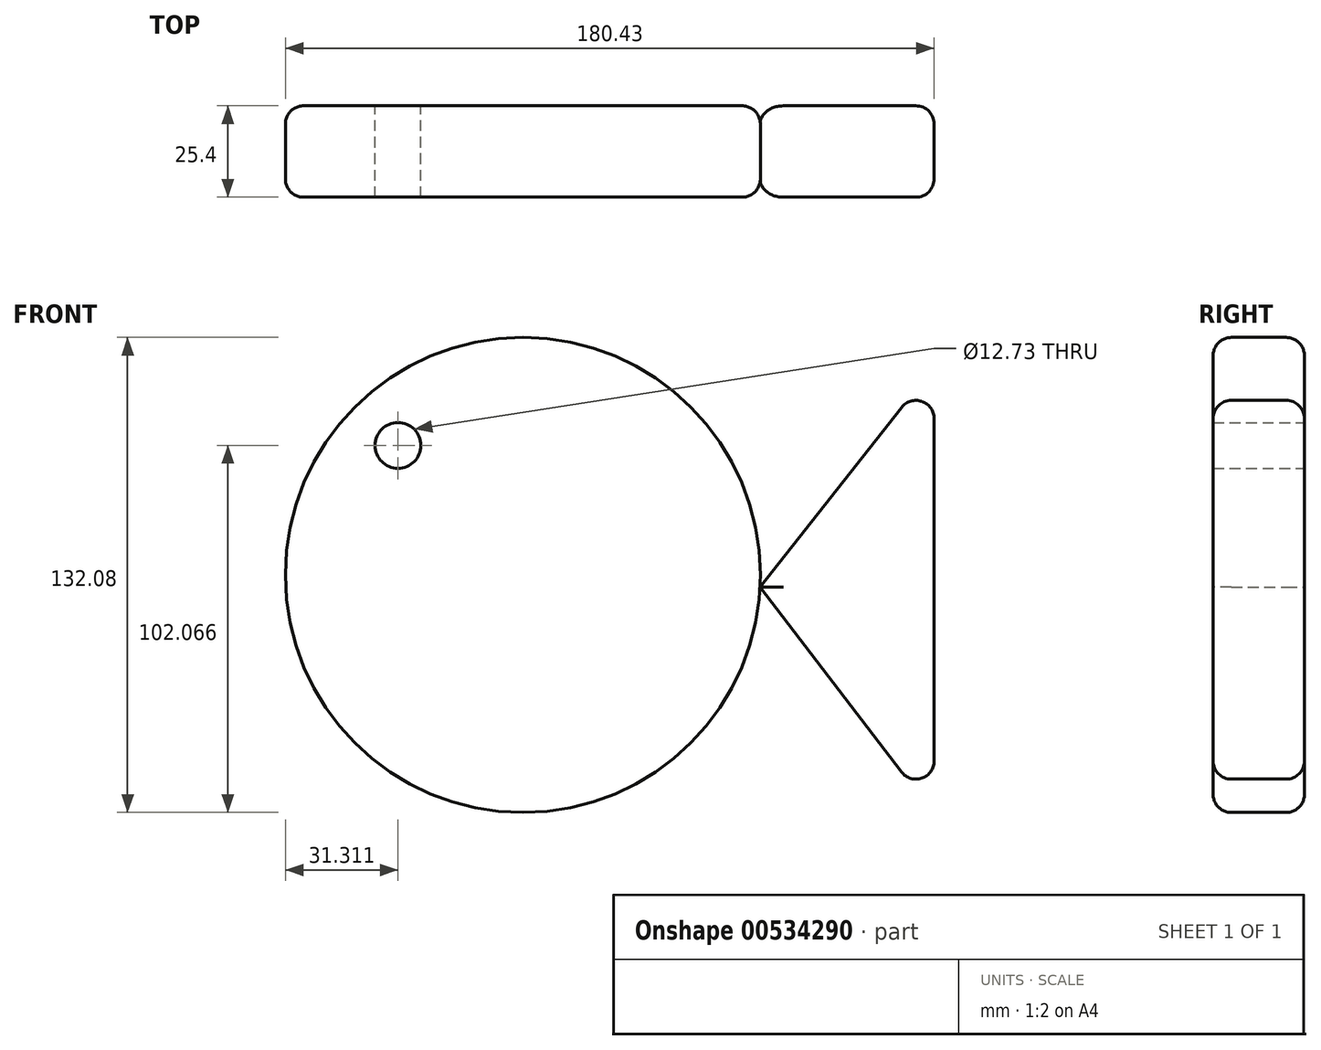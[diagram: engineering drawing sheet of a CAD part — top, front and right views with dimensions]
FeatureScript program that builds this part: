
annotation { "Feature Type Name" : "Feature", "Feature Type Description" : "" }
export const myFeature = defineFeature(function(context is Context, id is Id, definition is map)
    precondition{}
    {
        {
            var Q0;
            Q0=qCreatedBy(makeId("Front.planeOp"),FACE);
            var sketch = newSketch(context, id + "F0", { "sketchPlane" : qUnion([Q0])});
            skCircle(sketch, "E0", {"center": v(0, 0) * mm, "radius": 66.04 * mm});
            skLineSegment(sketch, "E1", {"start": v(65.95, -3.38) * mm, "end": v(114.39, 58.12) * mm});
            skLineSegment(sketch, "E2", {"start": v(114.39, 58.12) * mm, "end": v(114.39, -66.7) * mm});
            skLineSegment(sketch, "E3", {"start": v(114.39, -66.7) * mm, "end": v(65.95, -3.38) * mm});
            skSolve(sketch);
        }
        {
            var Q0;
            Q0=makeQuery(id+"F0.imprint","IMPRINT",FACE,{"disambiguationData":[TD([[makeQuery(id+"F0.imprint","IMPRINT",EDGE,{"derivedFrom":sQuery(id+"F0.wireOp",EDGE,"E0")}),1.0]])]});
            var Q1;
            Q1=makeQuery(id+"F0.imprint","IMPRINT",FACE,{"disambiguationData":[TD([[makeQuery(id+"F0.imprint","IMPRINT",EDGE,{"derivedFrom":sQuery(id+"F0.wireOp",EDGE,"E1")}),-1.0]])]});
            extrude(context, id + "F1", {"entities" : qUnion([Q0, Q1]), "depth" : 25.4 * mm, "offsetDistance" : 25.4 * mm});
        }
        {
            var Q0;
            Q0=makeQuery(id+"F1.opExtrude","CAP_EDGE",EDGE,{"disambiguationData":[OSD([sQuery(id+"F0.wireOp",EDGE,"E0")])],"isStart":false});
            var Q1;
            Q1=makeQuery(id+"F1.opExtrude","CAP_EDGE",EDGE,{"disambiguationData":[OSD([sQuery(id+"F0.wireOp",EDGE,"E0")])],"isStart":true});
            var Q2;
            Q2=makeQuery(id+"F1.opExtrude","CAP_EDGE",EDGE,{"disambiguationData":[OSD([sQuery(id+"F0.wireOp",EDGE,"E1")])],"isStart":false});
            var Q3;
            Q3=makeQuery(id+"F1.opExtrude","SWEPT_EDGE",EDGE,{"disambiguationData":[OSD([sQuery(id+"F0.wireOp",EDGE,"E1"),sQuery(id+"F0.wireOp",EDGE,"E2")])]});
            var Q4;
            Q4=makeQuery(id+"F1.opExtrude","CAP_EDGE",EDGE,{"disambiguationData":[OSD([sQuery(id+"F0.wireOp",EDGE,"E2")])],"isStart":true});
            var Q5;
            Q5=makeQuery(id+"F1.opExtrude","SWEPT_EDGE",EDGE,{"disambiguationData":[OSD([sQuery(id+"F0.wireOp",EDGE,"E2"),sQuery(id+"F0.wireOp",EDGE,"E3")])]});
            var Q6;
            Q6=makeQuery(id+"F1.opExtrude","CAP_EDGE",EDGE,{"disambiguationData":[OSD([sQuery(id+"F0.wireOp",EDGE,"E3")])],"isStart":false});
            var Q7;
            Q7=makeQuery(id+"F1.opExtrude","CAP_EDGE",EDGE,{"disambiguationData":[OSD([sQuery(id+"F0.wireOp",EDGE,"E2")])],"isStart":false});
            var Q8;
            Q8=makeQuery(id+"F1.opExtrude","CAP_EDGE",EDGE,{"disambiguationData":[OSD([sQuery(id+"F0.wireOp",EDGE,"E3")])],"isStart":true});
            var Q9;
            Q9=makeQuery(id+"F1.opExtrude","CAP_EDGE",EDGE,{"disambiguationData":[OSD([sQuery(id+"F0.wireOp",EDGE,"E1")])],"isStart":true});
            fillet(context, id + "F2", {"entities" : qUnion([Q0, Q1, Q2, Q3, Q4, Q5, Q6, Q7, Q8, Q9]), "radius" : 5.08 * mm, "tangentPropagation" : true, "allowEdgeOverflow" : false});
        }
        {
            var Q0;
            Q0=qCreatedBy(makeId("Front.planeOp"),FACE);
            var sketch = newSketch(context, id + "F3", { "sketchPlane" : qUnion([Q0])});
            skCircle(sketch, "E4", {"center": v(-34.73, 36.03) * mm, "radius": 6.37 * mm});
            skSolve(sketch);
        }
        {
            var Q0;
            Q0=makeQuery(id+"F3.imprint","IMPRINT",FACE,{"disambiguationData":[TD([[makeQuery(id+"F3.imprint","IMPRINT",EDGE,{"derivedFrom":sQuery(id+"F3.wireOp",EDGE,"E4")}),1.0]])]});
            extrude(context, id + "F4", {"entities" : qUnion([Q0]), "operationType" : NewBodyOperationType.REMOVE, "depth" : 25.4 * mm, "offsetDistance" : 25.4 * mm});
        }
    });
